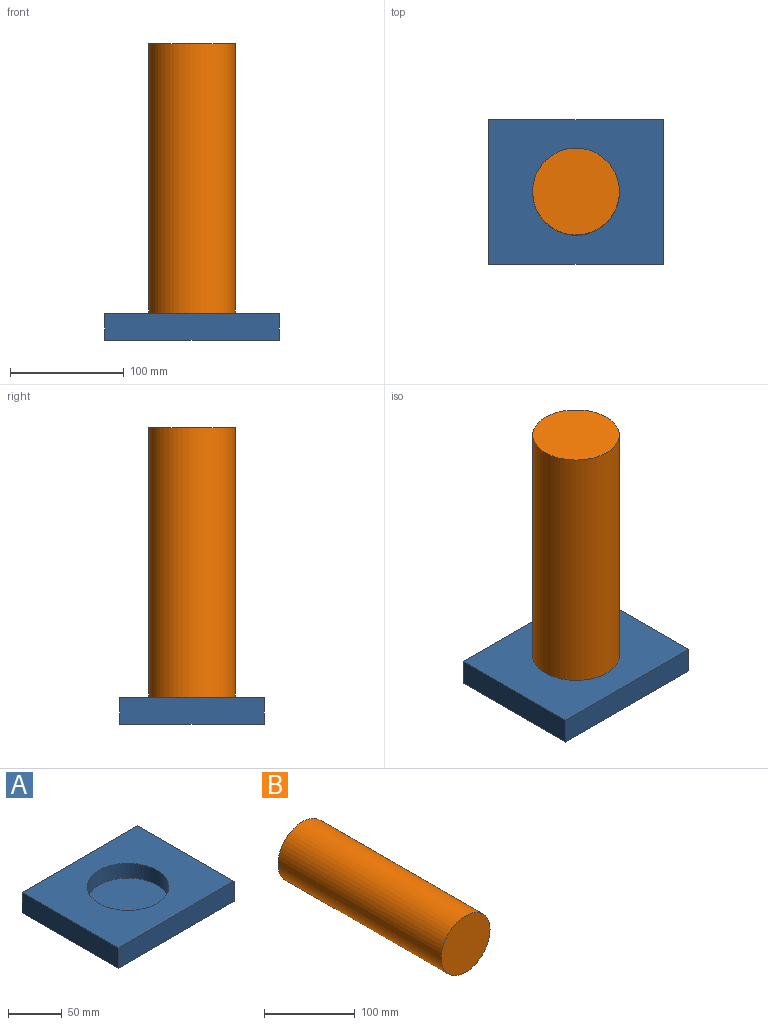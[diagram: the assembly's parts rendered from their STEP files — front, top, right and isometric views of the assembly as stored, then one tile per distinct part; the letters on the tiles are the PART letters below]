
ASSEMBLY  parts=2 mates=1
PART A: 8 faces, bbox 152.9x126.9x23.2 mm
  f0: plane 126.91x23.2mm, normal (1,0,0), area 2944.3mm2, adj f1,f3,f4,f5
  f1: plane 152.87x126.91mm, normal (0,0,1), area 14840.4mm2, adj f0,f2,f4,f5,f6
  f2: plane 126.91x23.2mm, normal (-1,0,0), area 2944.3mm2, adj f1,f3,f4,f5
  f3: plane 152.87x126.91mm, normal (0,0,-1), area 19400.8mm2, adj f0,f2,f4,f5
  f4: plane 152.87x23.2mm, normal (0,-1,0), area 3546.8mm2, adj f0,f1,f2,f3
  f5: plane 152.87x23.2mm, normal (0,1,0), area 3546.8mm2, adj f0,f1,f2,f3
  f6: cylinder r=38.1mm len=76.2mm, axis (0,0,1), area 4047.4mm2, adj f1,f7
  f7: plane 76.2x76.2mm, normal (0,0,1), area 4560.4mm2, adj f6
PART B: 3 faces, bbox 76.2x254x76.2 mm
  f0: cylinder r=38.1mm len=254mm, axis (0,1,0), area 60804.9mm2, adj f1,f2
  f1: plane 76.2x76.2mm, normal (0,-1,0), area 4560.4mm2, adj f0
  f2: plane 76.2x76.2mm, normal (0,1,0), area 4560.4mm2, adj f0
PLACE A t=(232.2,-40.13,-32.16)mm
PLACE B rot(axis=(0.43,-0.64,-0.64),133.5deg) t=(232.2,-40.13,89.54)mm
MATE revolute B.f0 <-> A.f6  axis (0,0,-1) through (232.2,-40.13,-37.46)mm
